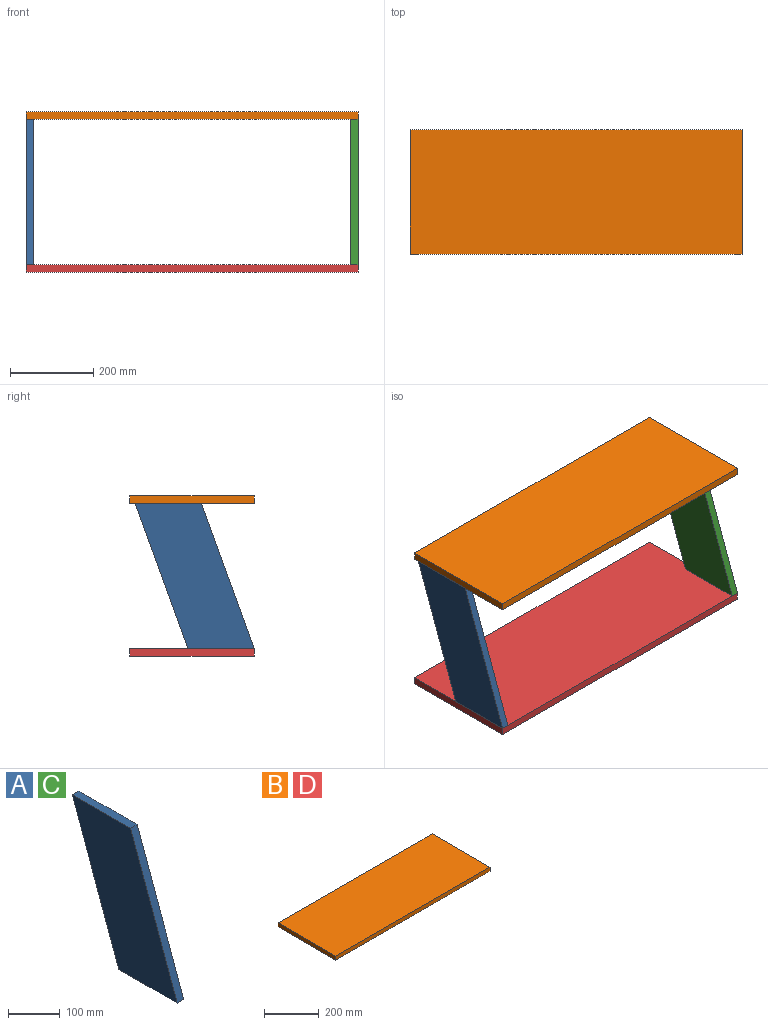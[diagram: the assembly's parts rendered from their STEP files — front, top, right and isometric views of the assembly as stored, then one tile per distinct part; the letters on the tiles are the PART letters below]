
ASSEMBLY  parts=4 mates=7
PART A: 6 faces, bbox 18x287x350 mm
  f0: plane 159.63x18mm, normal (0,0,-1), area 2873.3mm2, adj f1,f3,f4,f5
  f1: plane 350x127.39mm, normal (0,-0.94,0.34), area 6704.3mm2, adj f0,f2,f4,f5
  f2: plane 159.63x18mm, normal (0,0,1), area 2873.3mm2, adj f1,f3,f4,f5
  f3: plane 350x127.39mm, normal (0,0.94,-0.34), area 6704.3mm2, adj f0,f2,f4,f5
  f4: plane 350x287.02mm, normal (1,0,0), area 55869.3mm2, adj f0,f1,f2,f3
  f5: plane 350x287.02mm, normal (-1,0,0), area 55869.3mm2, adj f0,f1,f2,f3
PART B: 6 faces, bbox 800x300x18 mm
  f0: plane 800x300mm, normal (0,0,-1), area 240000mm2, adj f1,f3,f4,f5
  f1: plane 800x18mm, normal (0,1,0), area 14400mm2, adj f0,f2,f4,f5
  f2: plane 800x300mm, normal (0,0,1), area 240000mm2, adj f1,f3,f4,f5
  f3: plane 800x18mm, normal (0,-1,0), area 14400mm2, adj f0,f2,f4,f5
  f4: plane 300x18mm, normal (1,0,0), area 5400mm2, adj f0,f1,f2,f3
  f5: plane 300x18mm, normal (-1,0,0), area 5400mm2, adj f0,f1,f2,f3
PART C: same geometry as A
PART D: same geometry as B
PLACE A t=(-103.21,181.61,-253.71)mm
PLACE B t=(-103.21,181.61,114.29)mm
PLACE C t=(678.79,181.61,-253.71)mm
PLACE D t=(-103.21,181.61,-253.71)mm
MATE planar B.f3 <-> D.f3  axis (0,-1,0) through (296.79,-118.39,123.29)mm
MATE planar B.f0 <-> C.f2  axis (0,0,-1) through (296.79,31.61,114.29)mm
MATE planar B.f0 <-> A.f2  axis (0,0,-1) through (296.79,31.61,114.29)mm
MATE fastened A.f0 <-> D.f2  axis (0,0,1) through (-103.21,-118.39,-235.71)mm
MATE planar C.f0 <-> D.f2  axis (0,0,-1) through (687.79,-38.57,-235.71)mm
MATE fastened C.f0 <-> D.f2  axis (0,0,1) through (696.79,-118.39,-235.71)mm
MATE planar C.f4 <-> B.f4  axis (1,0,0) through (696.79,25.12,-60.71)mm
